# Revit family: towel holder 90_430
name_source: partatom
category: Furniture
units: mm (PartAtom-declared; Revit-internal decimal feet)

## family parameters
Always vertical = No
Cut with Voids When Loaded = No
OmniClass Number = 23.31.25.25
Room Calculation Point = No
Shared = Yes
Work Plane-Based = No

## types (6) — shared parameters
BASENUMBER = Towel holder 90/430
BIMOBJECT = Sanitary: Accessories
CATALOG = Hansgrohe
DESIGN = Germany
ETIM = Pr_40_20_76_90 | Towel rails
GTINCODE = 4059625458495
IFC = EC010551 | Towel holder
MASTERFORMAT = 10 28 00 | Toilet, Bath, and Laundry Accessories
Manufacturer = Hansgrohe
NAME = Xelu Q Towel holder 90/430
NBSYN = $BASENUMBER.-$ARTNR.--$SURFACE.-$LODLEVEL.
NN = Towel holder 90/430
OBJECTTYPE = Object (single object)
OMNICLASS = 23-31 25 25 | Towel Bars
PERMALINK = 54143XXX
PRODUCTFAMILY = Xelu Q
PRODUCTGROUP = Towel holder
PRODUCTURL = https://pro.hansgrohe.com
REGIONSET = Worldwide
SPECIFICATION = Surfaces:    - 54143000 Chrome  - 54143670 Matt Black  - 54143700 Matt White      Specification:    null
UNICLASS_2015_CODE = 40_20_76_90
UNIFORMATII = E2010 | Fixed Furnishings
UNSPSC = 301815 | Sanitary ware
WEIGHT = 0

## per-type parameters (varying)
| type | ARTNR | LINA | LODLEVEL | Model | NB | SURFACE |
| Towel holder 90_430-54143000--CHROME-200 | 54143000 | Towel holder 90/430-54143000--CHROME-200 | 200 | Towel holder 90/430-54143000--CHROME-200 | Towel holder 90/430-54143000--CHROME-200 | CHROME |
| Towel holder 90_430-54143000--CHROME-400 | 54143000 | Towel holder 90/430-54143000--CHROME-400 | 400 | Towel holder 90/430-54143000--CHROME-400 | Towel holder 90/430-54143000--CHROME-400 | CHROME |
| Towel holder 90_430-54143670--MATT_BLACK-200 | 54143670 | Towel holder 90/430-54143670--MATT_BLACK-200 | 200 | Towel holder 90/430-54143670--MATT_BLACK-200 | Towel holder 90/430-54143670--MATT_BLACK-200 | MATT_BLACK |
| Towel holder 90_430-54143670--MATT_BLACK-400 | 54143670 | Towel holder 90/430-54143670--MATT_BLACK-400 | 400 | Towel holder 90/430-54143670--MATT_BLACK-400 | Towel holder 90/430-54143670--MATT_BLACK-400 | MATT_BLACK |
| Towel holder 90_430-54143700--MATT_WHITE-200 | 54143700 | Towel holder 90/430-54143700--MATT_WHITE-200 | 200 | Towel holder 90/430-54143700--MATT_WHITE-200 | Towel holder 90/430-54143700--MATT_WHITE-200 | MATT_WHITE |
| Towel holder 90_430-54143700--MATT_WHITE-400 | 54143700 | Towel holder 90/430-54143700--MATT_WHITE-400 | 400 | Towel holder 90/430-54143700--MATT_WHITE-400 | Towel holder 90/430-54143700--MATT_WHITE-400 | MATT_WHITE |

type visibility flags: 6 boolean params named "<type name>_RX0RY0RZ0TX0TY0TZ0_V" — each type sets only its own to Yes (folded from table)

## geometry (parser evidence)
native form markers: Sweep x29
no freeform markers — native parametric forms only
